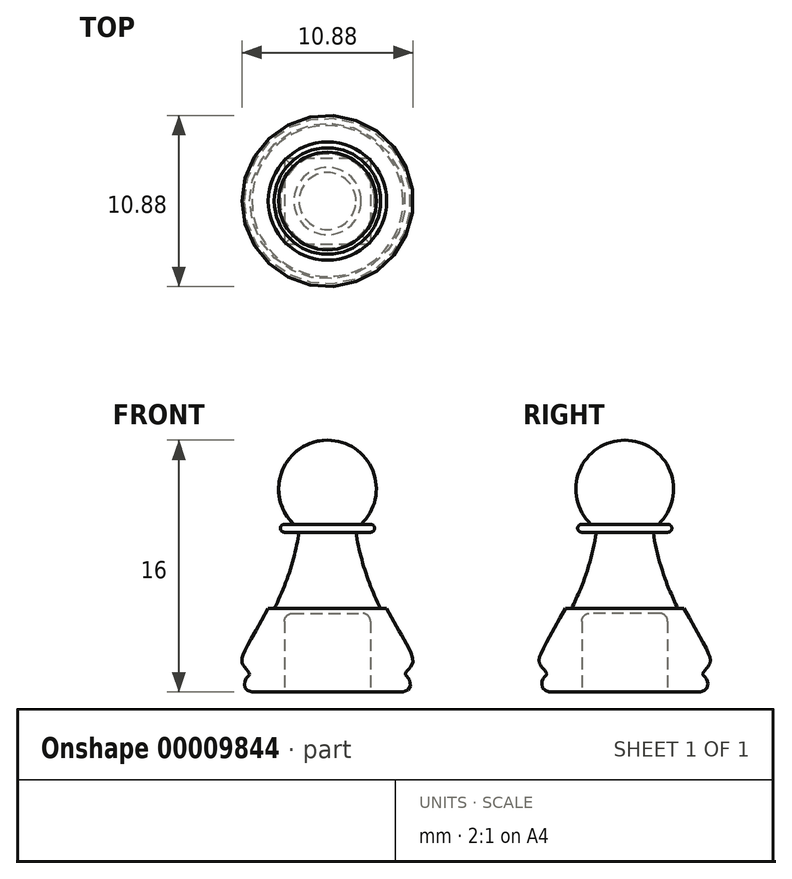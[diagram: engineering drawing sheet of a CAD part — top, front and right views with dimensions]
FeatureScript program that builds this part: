
annotation { "Feature Type Name" : "Feature", "Feature Type Description" : "" }
export const myFeature = defineFeature(function(context is Context, id is Id, definition is map)
    precondition{}
    {
        {
            var Q0;
            Q0=qCreatedBy(makeId("Front.planeOp"),FACE);
            var sketch = newSketch(context, id + "F0", { "sketchPlane" : qUnion([Q0])});
            skLineSegment(sketch, "E0", {"start": v(0, 24.13) * mm, "end": v(0, -0.78) * mm, "construction": true});
            skArc(sketch, "E1", {"start": v(0, 17.51) * mm, "mid": v(-2.88, 15.56) * mm, "end": v(-2.14, 12.17) * mm});
            skLineSegment(sketch, "E2.bottom", {"start": v(-2.74, 12.17) * mm, "end": v(-2.14, 12.17) * mm});
            skLineSegment(sketch, "E2.top", {"start": v(-2.74, 11.66) * mm, "end": v(-1.8, 11.66) * mm});
            skLineSegment(sketch, "E2.left", {"start": v(-2.99, 11.92) * mm, "end": v(-2.99, 11.91) * mm});
            skFitSpline(sketch, "E3", {"points": [v(-1.8, 11.66) * mm, v(-3.38, 6.81) * mm], "startDerivative": vector(-0.6, -4.53) * mm, "endDerivative": vector(-2.25, -4.45) * mm});
            skLineSegment(sketch, "E4", {"start": v(-3.38, 6.81) * mm, "end": v(-3.76, 6.81) * mm});
            skFitSpline(sketch, "E5", {"points": [v(-3.76, 6.81) * mm, v(-5.3, 3.15) * mm, v(-4.95, 2.65) * mm, v(-5.16, 2.4) * mm, v(-4.8, 1.51) * mm], "startDerivative": vector(-10.8, -19.06) * mm, "endDerivative": vector(7.88, -1.45) * mm});
            skLineSegment(sketch, "E6", {"start": v(-4.8, 1.51) * mm, "end": v(0, 1.51) * mm});
            skLineSegment(sketch, "E7", {"start": v(0, 17.51) * mm, "end": v(0, 1.51) * mm});
            skLineSegment(sketch, "E8", {"start": v(-5.44, 7.25) * mm, "end": v(-5.44, 2.65) * mm, "construction": true});
            skPoint(sketch, "E9.visualSharp", {"position": v(-2.99, 12.17) * mm});
            skArc(sketch, "E9.filletArc", {"start": v(-2.74, 12.17) * mm, "mid": v(-2.92, 12.1) * mm, "end": v(-2.99, 11.92) * mm});
            skPoint(sketch, "E10.visualSharp", {"position": v(-2.99, 11.66) * mm});
            skArc(sketch, "E10.filletArc", {"start": v(-2.99, 11.91) * mm, "mid": v(-2.92, 11.74) * mm, "end": v(-2.74, 11.66) * mm});
            skLineSegment(sketch, "E11", {"start": v(-3.1, 17.6) * mm, "end": v(-3.1, 10.4) * mm, "construction": true});
            skSolve(sketch);
        }
        {
            var Q0;
            Q0=qCreatedBy(makeId("Top.planeOp"),FACE);
            var sketch = newSketch(context, id + "F1", { "sketchPlane" : qUnion([Q0])});
            skCircle(sketch, "E12", {"center": v(0, 0) * mm, "radius": 29.84 * mm});
            skSolve(sketch);
        }
        {
            var Q0;
            Q0=makeQuery(id+"F0.imprint","IMPRINT",FACE,{"disambiguationData":[TD([[makeQuery(id+"F0.imprint","IMPRINT",EDGE,{"derivedFrom":sQuery(id+"F0.wireOp",EDGE,"E1")}),1.0]])]});
            var Q1;
            Q1=sQuery(id+"F1.wireOp",EDGE,"E12");
            sweep(context, id + "F2", {"profiles" : qUnion([Q0]), "path" : qUnion([Q1])});
        }
        {
            var Q0;
            Q0=makeQuery(id+"F2.opSweep","SWEPT_FACE",FACE,{"disambiguationData":[OSD([sQuery(id+"F0.wireOp",EDGE,"E6"),sQuery(id+"F1.wireOp",EDGE,"E12")])]});
            var sketch = newSketch(context, id + "F3", { "sketchPlane" : qUnion([Q0])});
            skLineSegment(sketch, "E13.bottom", {"start": v(-2.73, -2.72) * mm, "end": v(2.73, -2.73) * mm});
            skLineSegment(sketch, "E13.top", {"start": v(-2.73, 2.73) * mm, "end": v(2.73, 2.72) * mm});
            skLineSegment(sketch, "E13.left", {"start": v(-2.73, -2.72) * mm, "end": v(-2.73, 2.72) * mm});
            skLineSegment(sketch, "E13.right", {"start": v(2.73, -2.72) * mm, "end": v(2.73, 2.72) * mm});
            skLineSegment(sketch, "E14", {"start": v(0, -2.73) * mm, "end": v(0, 2.73) * mm, "construction": true});
            skLineSegment(sketch, "E15", {"start": v(-2.73, 0) * mm, "end": v(2.73, 0) * mm, "construction": true});
            skPoint(sketch, "E16", {"position": v(0, 0) * mm});
            skSolve(sketch);
        }
        {
            var Q0;
            Q0 = qSketchRegion(id + "F3", true);
            extrude(context, id + "F4", {"entities" : qUnion([Q0]), "operationType" : NewBodyOperationType.REMOVE, "oppositeDirection" : true, "depth" : 5 * mm});
        }
        {
            var Q0;
            Q0=makeQuery(id+"F4.boolean.opBoolean","COPY",FACE,{"derivedFrom":makeQuery(id+"F4.opExtrude","CAP_FACE",FACE,{"disambiguationData":[OSD([sQuery(id+"F3.wireOp",EDGE,"E13.bottom"),sQuery(id+"F3.wireOp",EDGE,"E13.top"),sQuery(id+"F3.wireOp",EDGE,"E13.left"),sQuery(id+"F3.wireOp",EDGE,"E13.right")])],"isStart":false})});
            fillet(context, id + "F5", {"entities" : qUnion([Q0]), "radius" : 0.5 * mm, "tangentPropagation" : true, "allowEdgeOverflow" : false});
        }
    });
